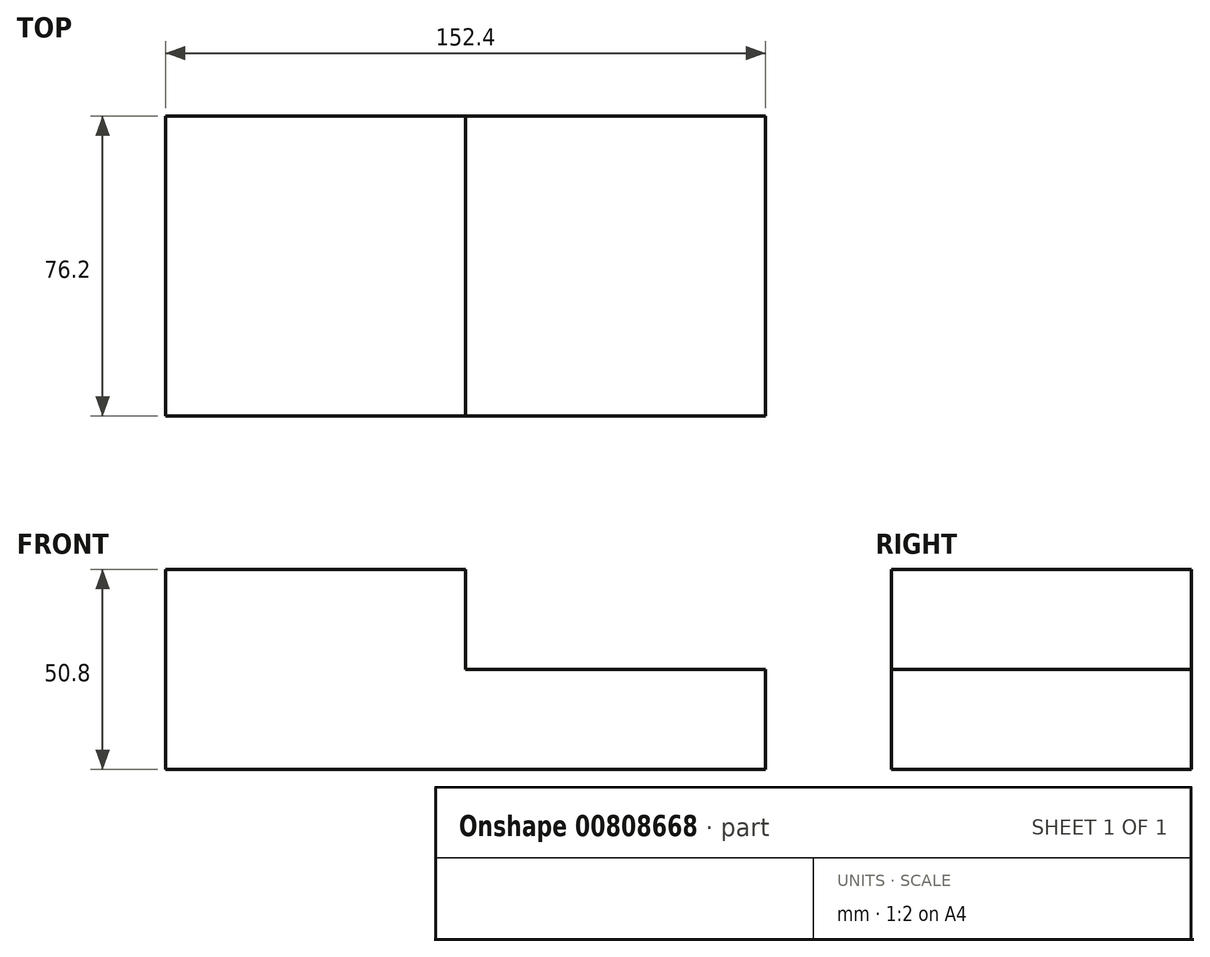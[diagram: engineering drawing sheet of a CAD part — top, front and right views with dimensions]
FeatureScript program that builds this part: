
annotation { "Feature Type Name" : "Feature", "Feature Type Description" : "" }
export const myFeature = defineFeature(function(context is Context, id is Id, definition is map)
    precondition{}
    {
        {
            var Q0;
            Q0=qCreatedBy(makeId("Front.planeOp"),FACE);
            var sketch = newSketch(context, id + "F0", { "sketchPlane" : qUnion([Q0])});
            skLineSegment(sketch, "E0", {"start": v(0, 0) * mm, "end": v(152.4, 0) * mm});
            skLineSegment(sketch, "E1", {"start": v(152.4, 0) * mm, "end": v(152.4, 25.4) * mm});
            skLineSegment(sketch, "E2", {"start": v(152.4, 25.4) * mm, "end": v(76.2, 25.4) * mm});
            skLineSegment(sketch, "E3", {"start": v(76.2, 25.4) * mm, "end": v(76.2, 50.8) * mm});
            skLineSegment(sketch, "E4", {"start": v(76.2, 50.8) * mm, "end": v(0, 50.8) * mm});
            skLineSegment(sketch, "E5", {"start": v(0, 50.8) * mm, "end": v(0, 0) * mm});
            skSolve(sketch);
        }
        {
            var Q0;
            Q0=makeQuery(id+"F0.imprint","IMPRINT",FACE,{"disambiguationData":[TD([[makeQuery(id+"F0.imprint","IMPRINT",EDGE,{"derivedFrom":sQuery(id+"F0.wireOp",EDGE,"E0")}),1.0]])]});
            extrude(context, id + "F1", {"entities" : qUnion([Q0]), "depth" : 76.2 * mm, "offsetDistance" : 25.4 * mm});
        }
    });
